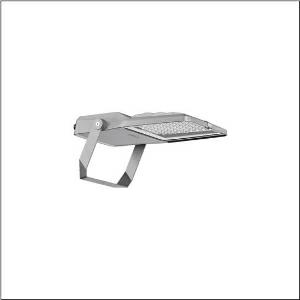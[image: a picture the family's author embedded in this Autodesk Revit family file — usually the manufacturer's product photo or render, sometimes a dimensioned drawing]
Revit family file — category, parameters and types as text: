
# Revit family: floodlight_fl_21_mini___pl52_5xa7773c2d1a_dd61
name_source: partatom
category: Lighting Fixtures
units: mm (PartAtom-declared; Revit-internal decimal feet)

## family parameters
Cut with Voids When Loaded = No
Host = Face
Light Source = No
Part Type = Normal
Room Calculation Point = No
Round Connector Dimension = Use Diameter
Shared = No

## types (1)
- --- (1 x LED, 19510 lm, 163.5 W, 3000K)
    Apparent Load = 163 VA
    CIE Flux Codes = 26 60 98 100 100
    Color Rendering = 70
    Color Temperature = 3000K
    Default Elevation = 1800 mm
    Description = Floodlight FL 21 mini, floodlight, primary light control with lens, of PMMA, primary optical cover: protective disc, of toughened safety glass, transparent, light distribution: PL52, light emission: direct distribution, installation type: surface-mounted, LED, High Power LED, rated luminous flux: 19.510lm, luminous efficacy: 119lm/W, light colour: 730, colour temperature: 3000K, control gear: ON/OFF Multilumen, control: Temp-Guard, with terminal, 6-pole, mains connection: 220..240V, AC, 50/60Hz, start of lifetime: 164W, luminaire housing, of diecast aluminium, powder-coated, Siteco® metallic grey (DB 702S), corrosivity category C5 mid according to DIN EN ISO 12944, suitable for swimming pools, chlorine-resistant, sealing non-destructively replaceable, mounting bracket, of steel, galvanised, powder-coated, Siteco® metallic grey (DB 702S), ON/OFF, protection rating (complete): IP66, insulation class (complete): insulation class I (protective earthing), certification: CE, ENEC, VDE, protection symbol: D, impact resistance: IK08, permissible operating ambient temperature: -40..+40°C, permissible operating ambient temperature for outdoor applications: -40..+50°C, standard: DIN EN 12944, LABS conformity tested according to VDMA 24364:2018-05, packaging unit: 1 piece

Light Distribution: PL52
    Height = 70 mm
    Lamp = 1 x LED
    Lamp Light Flux = 19510 lm
    Lamp Power = 163.5 W
    Lamp count = 1
    Length = 485 mm
    Luminous efficacy = 119 lm/W
    Manufacturer = Siteco
    ModVariant = No
    Model = 5XA7773C2D1A
    Number of Poles = 1
    OnlyDefault = Yes
    Power Factor = 1
    Product Name = Floodlight FL 21 mini | PL52
    Product group = floodlight | pylon annexe
    ProductGroupID = 6200
    Protection Class = Protection class I
    Protection Degree = IP 66
    RLX_Detail_Level = 1
    RLX_Emergency_Light_Flux = 0 lm
    RLX_Emergency_Type = 0
    RLX_Emergency_Type_DB = No
    RlxData = <blob elided: 94497 chars, md5=b2a9faed>
    Socket = socket
    Standby Power = 0 W
    System Light Flux = 19510 lm
    System Power = 163 W
    Type Comments = factory setting: luminous flux: 100 % | (ON | - | - | - | - | - | - | -) | 825 mA
    Type Image = l_1006845.jpg
    URL = http://relux.com
    VarID = @adj_164108
    Voltage = 0 V
    Weight = 0.00 kg
    Width = 337 mm

## geometry (parser evidence)
native form markers: Blend x4, Sweep x12
no freeform markers — native parametric forms only
